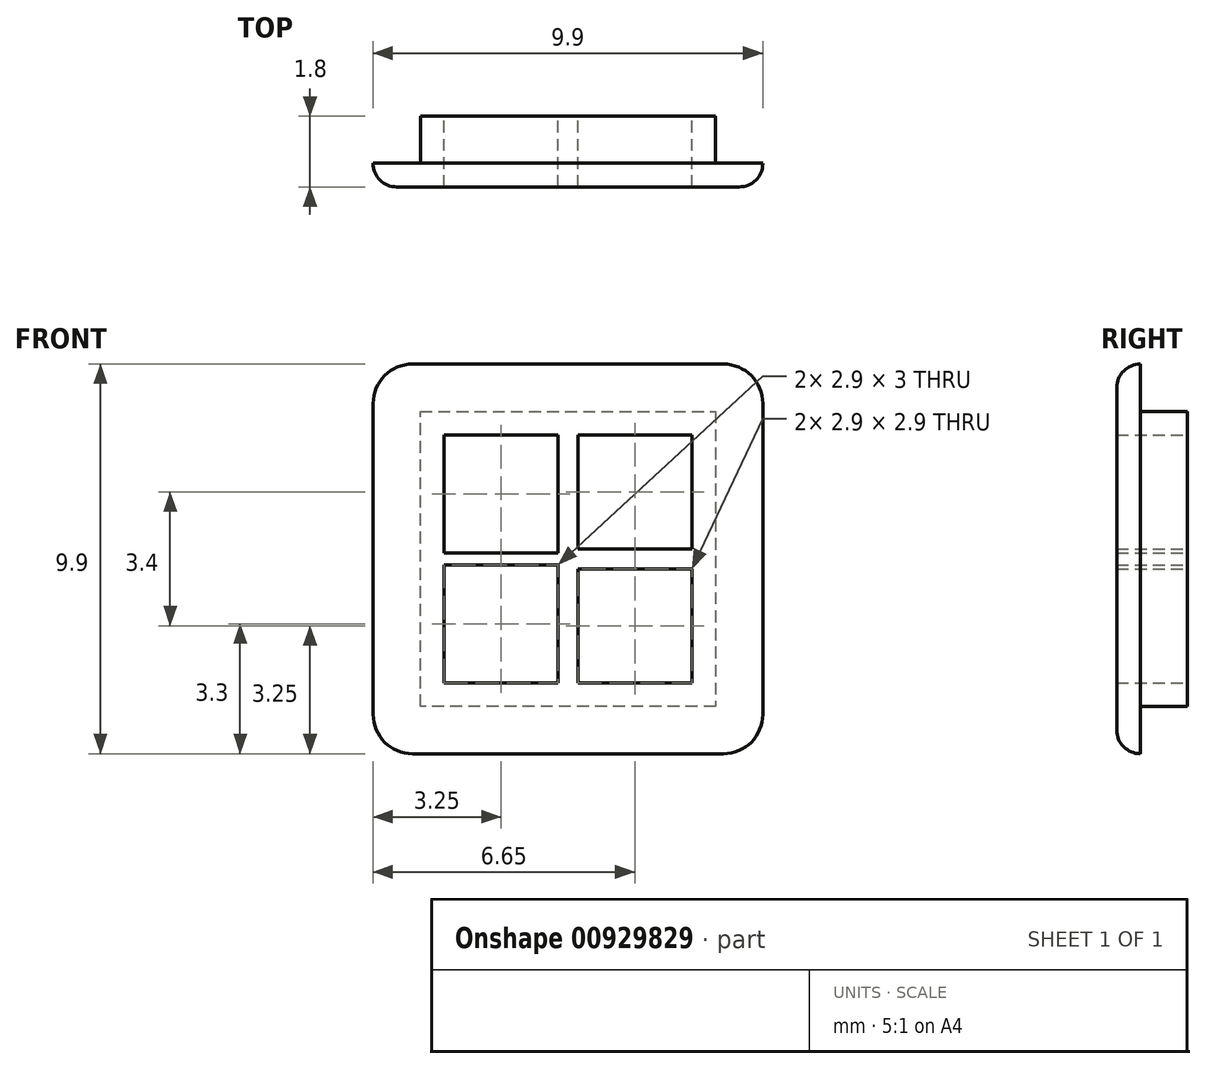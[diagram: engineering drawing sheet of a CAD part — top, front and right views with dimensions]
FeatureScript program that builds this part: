
annotation { "Feature Type Name" : "Feature", "Feature Type Description" : "" }
export const myFeature = defineFeature(function(context is Context, id is Id, definition is map)
    precondition{}
    {
        {
            var Q0;
            Q0=qCreatedBy(makeId("Front.planeOp"),FACE);
            var sketch = newSketch(context, id + "F0", { "sketchPlane" : qUnion([Q0])});
            skLineSegment(sketch, "E0.bottom", {"start": v(0, 0) * mm, "end": v(3, 0) * mm});
            skLineSegment(sketch, "E0.top", {"start": v(0, 3) * mm, "end": v(3, 3) * mm});
            skLineSegment(sketch, "E0.left", {"start": v(0, 0) * mm, "end": v(0, 3) * mm});
            skLineSegment(sketch, "E0.right", {"start": v(3, 0) * mm, "end": v(3, 3) * mm});
            skLineSegment(sketch, "E1", {"start": v(0, 3) * mm, "end": v(0, 3.3) * mm});
            skLineSegment(sketch, "E2", {"start": v(0, 3.3) * mm, "end": v(-0.3, 3.3) * mm});
            skLineSegment(sketch, "E3.bottom", {"start": v(0, 3.3) * mm, "end": v(3, 3.3) * mm});
            skLineSegment(sketch, "E3.top", {"start": v(0, 6.3) * mm, "end": v(3, 6.3) * mm});
            skLineSegment(sketch, "E3.left", {"start": v(0, 3.3) * mm, "end": v(0, 6.3) * mm});
            skLineSegment(sketch, "E3.right", {"start": v(3, 3.3) * mm, "end": v(3, 6.3) * mm});
            skLineSegment(sketch, "E4.bottom", {"start": v(-0.3, 3.3) * mm, "end": v(-3.3, 3.3) * mm});
            skLineSegment(sketch, "E4.top", {"start": v(-0.3, 6.3) * mm, "end": v(-3.3, 6.3) * mm});
            skLineSegment(sketch, "E4.left", {"start": v(-0.3, 3.3) * mm, "end": v(-0.3, 6.3) * mm});
            skLineSegment(sketch, "E4.right", {"start": v(-3.3, 3.3) * mm, "end": v(-3.3, 6.3) * mm});
            skLineSegment(sketch, "E5.bottom", {"start": v(-0.3, 3) * mm, "end": v(-3.3, 3) * mm});
            skLineSegment(sketch, "E5.top", {"start": v(-0.3, 0) * mm, "end": v(-3.3, 0) * mm});
            skLineSegment(sketch, "E5.left", {"start": v(-0.3, 3) * mm, "end": v(-0.3, 0) * mm});
            skLineSegment(sketch, "E5.right", {"start": v(-3.3, 3) * mm, "end": v(-3.3, 0) * mm});
            skLineSegment(sketch, "E6.bottom", {"start": v(3.6, 6.9) * mm, "end": v(-3.9, 6.9) * mm});
            skLineSegment(sketch, "E6.top", {"start": v(3.6, -0.6) * mm, "end": v(-3.9, -0.6) * mm});
            skLineSegment(sketch, "E6.left", {"start": v(3.6, 6.9) * mm, "end": v(3.6, -0.6) * mm});
            skLineSegment(sketch, "E6.right", {"start": v(-3.9, 6.9) * mm, "end": v(-3.9, -0.6) * mm});
            skLineSegment(sketch, "E7", {"start": v(-0.3, 6.3) * mm, "end": v(-0.4, 6.3) * mm});
            skLineSegment(sketch, "E8", {"start": v(-0.4, 6.3) * mm, "end": v(-0.4, 3.3) * mm});
            skLineSegment(sketch, "E9", {"start": v(0, 6.3) * mm, "end": v(0.1, 6.3) * mm});
            skLineSegment(sketch, "E10", {"start": v(0.1, 6.3) * mm, "end": v(0.1, 3.3) * mm});
            skLineSegment(sketch, "E11", {"start": v(0.1, 3) * mm, "end": v(0.1, 0) * mm});
            skLineSegment(sketch, "E12", {"start": v(-0.4, 3) * mm, "end": v(-0.4, 0) * mm});
            skLineSegment(sketch, "E13", {"start": v(-3.3, 3) * mm, "end": v(-3.3, 2.9) * mm});
            skLineSegment(sketch, "E14", {"start": v(-3.3, 2.9) * mm, "end": v(3, 2.9) * mm});
            skLineSegment(sketch, "E15", {"start": v(-3.3, 3.3) * mm, "end": v(-3.3, 3.4) * mm});
            skLineSegment(sketch, "E16", {"start": v(-3.3, 3.4) * mm, "end": v(3, 3.4) * mm});
            skSolve(sketch);
        }
        {
            var Q0;
            Q0=makeQuery(id+"F0.imprint","IMPRINT",FACE,{"disambiguationData":[TD([[makeQuery(id+"F0.imprint","IMPRINT",EDGE,{"derivedFrom":sQuery(id+"F0.wireOp",EDGE,"E0.bottom")}),-1.0]])]});
            var Q1;
            {var subQ0=sQuery(id+"F0.wireOp",EDGE,"E4.left");Q1=makeQuery(id+"F0.imprint","IMPRINT",FACE,{"disambiguationData":[TD([[makeQuery(id+"F0.imprint","IMPRINT",EDGE,{"derivedFrom":subQ0}),1.0]])]});}
            var Q2;
            {var subQ0=sQuery(id+"F0.wireOp",EDGE,"E3.left");Q2=makeQuery(id+"F0.imprint","IMPRINT",FACE,{"disambiguationData":[TD([[makeQuery(id+"F0.imprint","IMPRINT",EDGE,{"derivedFrom":subQ0}),-1.0]])]});}
            var Q3;
            {var subQ0=sQuery(id+"F0.wireOp",EDGE,"E2");Q3=makeQuery(id+"F0.imprint","IMPRINT",FACE,{"disambiguationData":[TD([[makeQuery(id+"F0.imprint","IMPRINT",EDGE,{"derivedFrom":subQ0}),-1.0]])]});}
            var Q4;
            {var subQ0=sQuery(id+"F0.wireOp",EDGE,"E15");Q4=makeQuery(id+"F0.imprint","IMPRINT",FACE,{"disambiguationData":[TD([[makeQuery(id+"F0.imprint","IMPRINT",EDGE,{"derivedFrom":subQ0}),-1.0]])]});}
            var Q5;
            {var subQ0=sQuery(id+"F0.wireOp",EDGE,"E3.right");var subQ1=sQuery(id+"F0.wireOp",EDGE,"E3.bottom");var subQ2=makeQuery(id+"F0.imprint","INTERSECT",VERTEX,{"derivedFrom":[subQ1,subQ0]});Q5=makeQuery(id+"F0.imprint","IMPRINT",FACE,{"disambiguationData":[TD([[makeQuery(id+"F0.imprint","IMPRINT",EDGE,{"disambiguationData":[TD([[subQ2,1.0]])],"derivedFrom":subQ1}),1.0]])]});}
            var Q6;
            {var subQ0=sQuery(id+"F0.wireOp",EDGE,"E0.right");var subQ1=sQuery(id+"F0.wireOp",EDGE,"E0.top");var subQ2=makeQuery(id+"F0.imprint","INTERSECT",VERTEX,{"derivedFrom":[subQ1,subQ0]});Q6=makeQuery(id+"F0.imprint","IMPRINT",FACE,{"disambiguationData":[TD([[makeQuery(id+"F0.imprint","IMPRINT",EDGE,{"disambiguationData":[TD([[subQ2,1.0]])],"derivedFrom":subQ1}),-1.0]])]});}
            var Q7;
            {var subQ0=sQuery(id+"F0.wireOp",EDGE,"E13");Q7=makeQuery(id+"F0.imprint","IMPRINT",FACE,{"disambiguationData":[TD([[makeQuery(id+"F0.imprint","IMPRINT",EDGE,{"derivedFrom":subQ0}),1.0]])]});}
            var Q8;
            {var subQ0=sQuery(id+"F0.wireOp",EDGE,"E5.left");var subQ1=sQuery(id+"F0.wireOp",EDGE,"E5.top");var subQ2=makeQuery(id+"F0.imprint","INTERSECT",VERTEX,{"derivedFrom":[subQ1,subQ0]});Q8=makeQuery(id+"F0.imprint","IMPRINT",FACE,{"disambiguationData":[TD([[makeQuery(id+"F0.imprint","IMPRINT",EDGE,{"disambiguationData":[TD([[subQ2,-1.0]])],"derivedFrom":subQ1}),-1.0]])]});}
            var Q9;
            {var subQ0=sQuery(id+"F0.wireOp",EDGE,"E0.left");var subQ1=sQuery(id+"F0.wireOp",EDGE,"E0.bottom");var subQ2=makeQuery(id+"F0.imprint","INTERSECT",VERTEX,{"derivedFrom":[subQ1,subQ0]});Q9=makeQuery(id+"F0.imprint","IMPRINT",FACE,{"disambiguationData":[TD([[makeQuery(id+"F0.imprint","IMPRINT",EDGE,{"disambiguationData":[TD([[subQ2,-1.0]])],"derivedFrom":subQ1}),1.0]])]});}
            var Q10;
            {var subQ0=sQuery(id+"F0.wireOp",EDGE,"E0.left");var subQ1=sQuery(id+"F0.wireOp",EDGE,"E0.top");var subQ2=makeQuery(id+"F0.imprint","INTERSECT",VERTEX,{"derivedFrom":[subQ1,subQ0]});Q10=makeQuery(id+"F0.imprint","IMPRINT",FACE,{"disambiguationData":[TD([[makeQuery(id+"F0.imprint","IMPRINT",EDGE,{"disambiguationData":[TD([[subQ2,-1.0]])],"derivedFrom":subQ1}),-1.0]])]});}
            var Q11;
            {var subQ0=sQuery(id+"F0.wireOp",EDGE,"E5.left");var subQ1=sQuery(id+"F0.wireOp",EDGE,"E5.bottom");var subQ2=makeQuery(id+"F0.imprint","INTERSECT",VERTEX,{"derivedFrom":[subQ1,subQ0]});Q11=makeQuery(id+"F0.imprint","IMPRINT",FACE,{"disambiguationData":[TD([[makeQuery(id+"F0.imprint","IMPRINT",EDGE,{"disambiguationData":[TD([[subQ2,-1.0]])],"derivedFrom":subQ1}),1.0]])]});}
            extrude(context, id + "F1", {"entities" : qUnion([Q0, Q1, Q2, Q3, Q4, Q5, Q6, Q7, Q8, Q9, Q10, Q11]), "depth" : 1.8 * mm, "offsetDistance" : 25 * mm});
        }
        {
            var Q0;
            Q0=makeQuery(id+"F1.opExtrude","SWEPT_FACE",FACE,{"disambiguationData":[OSD([sQuery(id+"F0.wireOp",EDGE,"E6.right")])]});
            var sketch = newSketch(context, id + "F2", { "sketchPlane" : qUnion([Q0])});
            skLineSegment(sketch, "E17.bottom", {"start": v(1.8, -0.6) * mm, "end": v(1.2, -0.6) * mm});
            skLineSegment(sketch, "E17.top", {"start": v(1.8, 6.9) * mm, "end": v(1.2, 6.9) * mm});
            skLineSegment(sketch, "E17.left", {"start": v(1.8, -0.6) * mm, "end": v(1.8, 6.9) * mm});
            skLineSegment(sketch, "E17.right", {"start": v(1.2, -0.6) * mm, "end": v(1.2, 6.9) * mm});
            skSolve(sketch);
        }
        {
            var Q0;
            Q0=makeQuery(id+"F2.imprint","IMPRINT",FACE,{"disambiguationData":[TD([[makeQuery(id+"F2.imprint","IMPRINT",EDGE,{"derivedFrom":sQuery(id+"F2.wireOp",EDGE,"E17.bottom")}),-1.0]])]});
            extrude(context, id + "F3", {"entities" : qUnion([Q0]), "operationType" : NewBodyOperationType.ADD, "depth" : 1.2 * mm, "offsetDistance" : 25 * mm});
        }
        {
            var Q0;
            Q0=makeQuery(id+"F1.opExtrude","SWEPT_FACE",FACE,{"disambiguationData":[OSD([sQuery(id+"F0.wireOp",EDGE,"E6.left")])]});
            var sketch = newSketch(context, id + "F4", { "sketchPlane" : qUnion([Q0])});
            skLineSegment(sketch, "E18.left", {"start": v(-1.8, 6.9) * mm, "end": v(-1.8, -0.6) * mm});
            skLineSegment(sketch, "E19", {"start": v(-1.8, 6.9) * mm, "end": v(-1.2, 6.9) * mm});
            skLineSegment(sketch, "E20", {"start": v(-1.2, 6.9) * mm, "end": v(-1.2, -0.6) * mm});
            skLineSegment(sketch, "E21", {"start": v(-1.2, -0.6) * mm, "end": v(-1.8, -0.6) * mm});
            skSolve(sketch);
        }
        {
            var Q0;
            Q0=makeQuery(id+"F4.imprint","IMPRINT",FACE,{"disambiguationData":[TD([[makeQuery(id+"F4.imprint","IMPRINT",EDGE,{"derivedFrom":sQuery(id+"F4.wireOp",EDGE,"E18.left")}),1.0]])]});
            extrude(context, id + "F5", {"entities" : qUnion([Q0]), "operationType" : NewBodyOperationType.ADD, "depth" : 1.2 * mm, "offsetDistance" : 25 * mm});
        }
        {
            var Q0;
            Q0=makeQuery(id+"F5.boolean.opBoolean","MERGE",FACE,{"derivedFrom":[makeQuery(id+"F3.boolean.opBoolean","MERGE",FACE,{"derivedFrom":[makeQuery(id+"F1.opExtrude","SWEPT_FACE",FACE,{"disambiguationData":[OSD([sQuery(id+"F0.wireOp",EDGE,"E6.bottom")])]}),makeQuery(id+"F3.opExtrude","SWEPT_FACE",FACE,{"disambiguationData":[OSD([sQuery(id+"F2.wireOp",EDGE,"LJDu7vXA-MeX7-wxbn-sf1F-hPuP9tR1u4d2")])]})]}),makeQuery(id+"F5.opExtrude","SWEPT_FACE",FACE,{"disambiguationData":[OSD([sQuery(id+"F4.wireOp",EDGE,"E19")])]})]});
            var sketch = newSketch(context, id + "F6", { "sketchPlane" : qUnion([Q0])});
            skLineSegment(sketch, "E22.left", {"start": v(4.8, -1.8) * mm, "end": v(4.8, -1.8) * mm});
            skLineSegment(sketch, "E22.right", {"start": v(-5.1, -1.23) * mm, "end": v(-5.1, -1.2) * mm});
            skLineSegment(sketch, "E23.bottom", {"start": v(4.8, -1.8) * mm, "end": v(-5.1, -1.8) * mm});
            skLineSegment(sketch, "E23.left", {"start": v(4.8, -1.8) * mm, "end": v(4.8, -1.2) * mm});
            skLineSegment(sketch, "E23.right", {"start": v(-5.1, -1.8) * mm, "end": v(-5.1, -1.2) * mm});
            skLineSegment(sketch, "E24", {"start": v(-5.1, -1.2) * mm, "end": v(4.8, -1.2) * mm});
            skSolve(sketch);
        }
        {
            var Q0;
            {var subQ0=sQuery(id+"F6.wireOp",EDGE,"E23.right");Q0=makeQuery(id+"F6.imprint","IMPRINT",FACE,{"disambiguationData":[TD([[makeQuery(id+"F6.imprint","IMPRINT",EDGE,{"derivedFrom":subQ0}),-1.0]])]});}
            extrude(context, id + "F7", {"entities" : qUnion([Q0]), "operationType" : NewBodyOperationType.ADD, "depth" : 1.2 * mm, "offsetDistance" : 25 * mm});
        }
        {
            var Q0;
            Q0=makeQuery(id+"F5.boolean.opBoolean","MERGE",FACE,{"derivedFrom":[makeQuery(id+"F3.boolean.opBoolean","MERGE",FACE,{"derivedFrom":[makeQuery(id+"F1.opExtrude","SWEPT_FACE",FACE,{"disambiguationData":[OSD([sQuery(id+"F0.wireOp",EDGE,"E6.top")])]}),makeQuery(id+"F3.opExtrude","SWEPT_FACE",FACE,{"disambiguationData":[OSD([sQuery(id+"F2.wireOp",EDGE,"o3IN3gTb-Kc8a-OEb0-BJQq-A7R68qGGokcf.bottom")])]})]}),makeQuery(id+"F5.opExtrude","SWEPT_FACE",FACE,{"disambiguationData":[OSD([sQuery(id+"F4.wireOp",EDGE,"E18.top")])]})]});
            var sketch = newSketch(context, id + "F8", { "sketchPlane" : qUnion([Q0])});
            skLineSegment(sketch, "E25.bottom", {"start": v(4.8, 1.2) * mm, "end": v(-5.1, 1.2) * mm});
            skLineSegment(sketch, "E25.top", {"start": v(4.8, 1.8) * mm, "end": v(-5.1, 1.8) * mm});
            skLineSegment(sketch, "E25.left", {"start": v(4.8, 1.2) * mm, "end": v(4.8, 1.8) * mm});
            skLineSegment(sketch, "E25.right", {"start": v(-5.1, 1.2) * mm, "end": v(-5.1, 1.8) * mm});
            skSolve(sketch);
        }
        {
            var Q0;
            Q0=makeQuery(id+"F8.imprint","IMPRINT",FACE,{"disambiguationData":[TD([[makeQuery(id+"F8.imprint","IMPRINT",EDGE,{"derivedFrom":sQuery(id+"F8.wireOp",EDGE,"E25.top")}),1.0]])]});
            extrude(context, id + "F9", {"entities" : qUnion([Q0]), "operationType" : NewBodyOperationType.ADD, "depth" : 1.2 * mm, "offsetDistance" : 25 * mm});
        }
        {
            var Q0;
            Q0=makeQuery(id+"F9.opExtrude","CAP_EDGE",EDGE,{"disambiguationData":[OSD([sQuery(id+"F8.wireOp",EDGE,"E25.right")])],"isStart":false});
            var Q1;
            Q1=makeQuery(id+"F9.opExtrude","CAP_EDGE",EDGE,{"disambiguationData":[OSD([sQuery(id+"F8.wireOp",EDGE,"E25.left")])],"isStart":false});
            var Q2;
            Q2=makeQuery(id+"F7.opExtrude","CAP_EDGE",EDGE,{"disambiguationData":[OSD([sQuery(id+"F6.wireOp",EDGE,"E23.left")])],"isStart":false});
            var Q3;
            Q3=makeQuery(id+"F7.opExtrude","CAP_EDGE",EDGE,{"disambiguationData":[OSD([sQuery(id+"F6.wireOp",EDGE,"E23.right")])],"isStart":false});
            fillet(context, id + "F10", {"entities" : qUnion([Q0, Q1, Q2, Q3]), "radius" : 1 * mm, "tangentPropagation" : true, "allowEdgeOverflow" : false});
        }
        {
            var Q0;
            Q0=makeQuery(id+"F9.boolean.opBoolean","MERGE",EDGE,{"derivedFrom":[makeQuery(id+"F7.boolean.opBoolean","MERGE",EDGE,{"derivedFrom":[makeQuery(id+"F3.opExtrude","CAP_EDGE",EDGE,{"disambiguationData":[OSD([sQuery(id+"F2.wireOp",EDGE,"E17.left")])],"isStart":false}),makeQuery(id+"F7.opExtrude","SWEPT_EDGE",EDGE,{"disambiguationData":[OSD([sQuery(id+"F6.wireOp",EDGE,"E23.bottom"),sQuery(id+"F6.wireOp",EDGE,"E23.right")])]})]}),makeQuery(id+"F9.opExtrude","SWEPT_EDGE",EDGE,{"disambiguationData":[OSD([sQuery(id+"F8.wireOp",EDGE,"E25.top"),sQuery(id+"F8.wireOp",EDGE,"E25.right")])]})]});
            fillet(context, id + "F11", {"entities" : qUnion([Q0]), "radius" : .6 * mm, "tangentPropagation" : true, "allowEdgeOverflow" : false});
        }
    });
